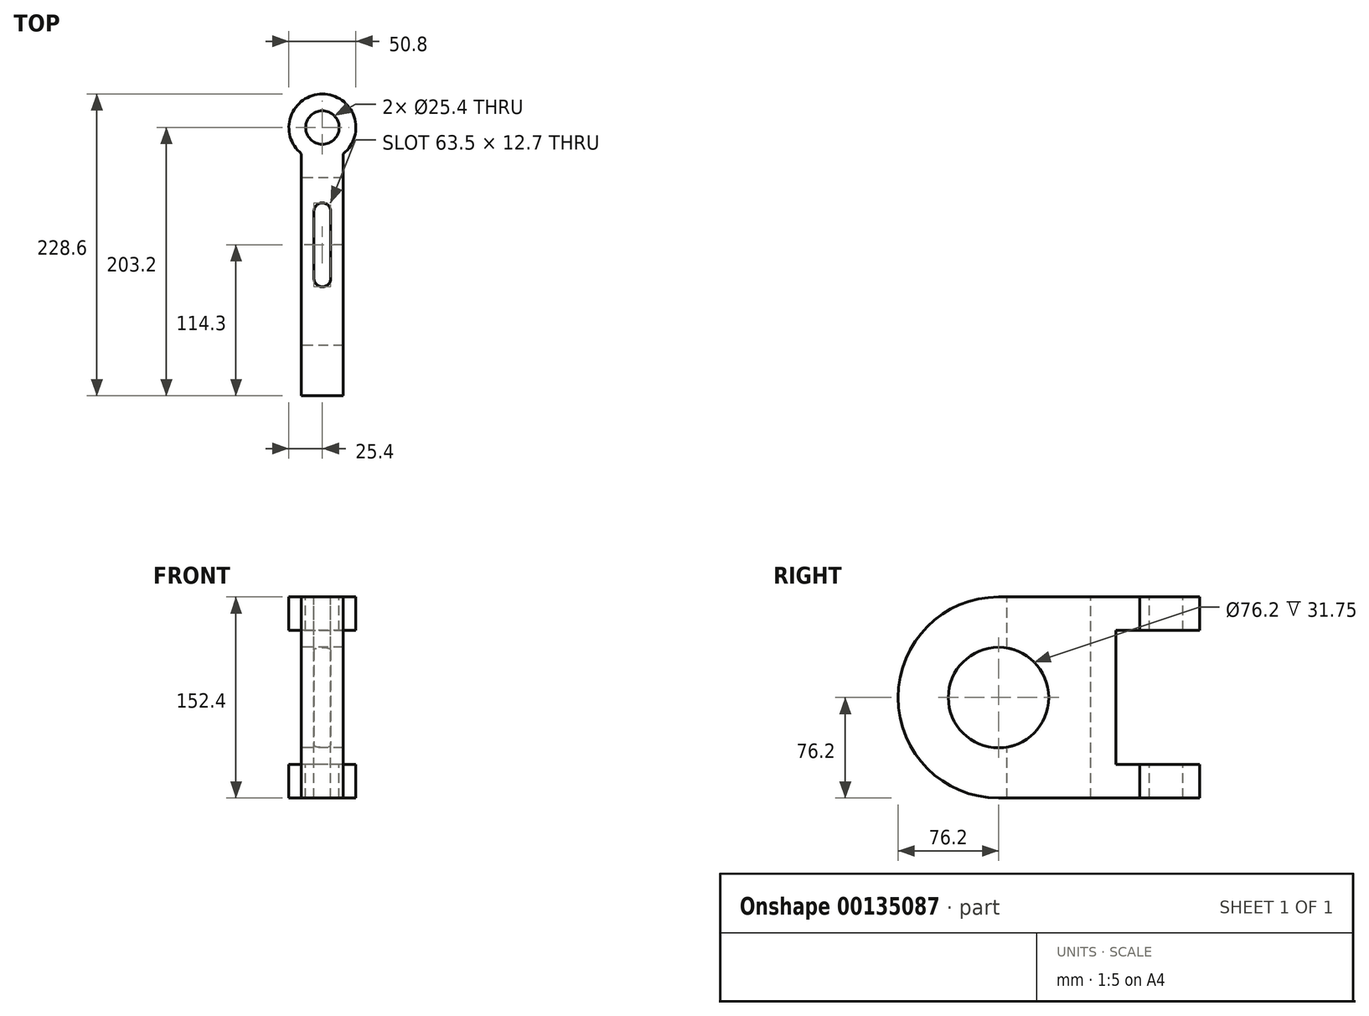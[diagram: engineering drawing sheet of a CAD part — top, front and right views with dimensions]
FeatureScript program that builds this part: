
annotation { "Feature Type Name" : "Feature", "Feature Type Description" : "" }
export const myFeature = defineFeature(function(context is Context, id is Id, definition is map)
    precondition{}
    {
        {
            var Q0;
            Q0=qCreatedBy(makeId("Right.planeOp"),FACE);
            var sketch = newSketch(context, id + "F0", { "sketchPlane" : qUnion([Q0])});
            skCircle(sketch, "E0", {"center": v(0, 0) * mm, "radius": 38.1 * mm});
            skArc(sketch, "E1", {"start": v(0, 76.2) * mm, "mid": v(-76.2, 0) * mm, "end": v(0, -76.2) * mm});
            skPoint(sketch, "E2", {"position": v(88.9, 0) * mm});
            skLineSegment(sketch, "E3", {"start": v(0, 76.2) * mm, "end": v(114.3, 76.2) * mm});
            skLineSegment(sketch, "E4", {"start": v(88.9, 50.8) * mm, "end": v(88.9, -50.8) * mm});
            skLineSegment(sketch, "E5", {"start": v(114.3, 76.2) * mm, "end": v(114.3, 50.8) * mm});
            skLineSegment(sketch, "E6", {"start": v(114.3, 50.8) * mm, "end": v(88.9, 50.8) * mm});
            skLineSegment(sketch, "E7", {"start": v(-76.2, 0) * mm, "end": v(76.2, 0) * mm, "construction": true});
            skLineSegment(sketch, "E8.MirrorCS", {"start": v(114.3, -76.2) * mm, "end": v(114.3, -50.8) * mm});
            skLineSegment(sketch, "E9.MirrorCS", {"start": v(114.3, -50.8) * mm, "end": v(88.9, -50.8) * mm});
            skLineSegment(sketch, "E10.MirrorCS", {"start": v(0, -76.2) * mm, "end": v(114.3, -76.2) * mm});
            skSolve(sketch);
        }
        {
            var Q0;
            Q0 = qSketchRegion(id + "F0", true);
            extrude(context, id + "F1", {"entities" : qUnion([Q0]), "depth" : 15.88 * mm, "hasSecondDirection" : true, "secondDirectionOppositeDirection" : true, "secondDirectionDepth" : 15.88 * mm});
        }
        {
            var Q0;
            Q0=makeQuery(id+"F1.opExtrude","SWEPT_FACE",FACE,{"disambiguationData":[OSD([sQuery(id+"F0.wireOp",EDGE,"E3")])]});
            var sketch = newSketch(context, id + "F2", { "sketchPlane" : qUnion([Q0])});
            skPoint(sketch, "E11", {"position": v(0, 152.4) * mm});
            skPoint(sketch, "E11.positionSnap0", {"position": v(0, 114.3) * mm});
            skPoint(sketch, "E12", {"position": v(0, 127) * mm});
            skArc(sketch, "E13", {"start": v(15.88, 107.17) * mm, "mid": v(0, 152.4) * mm, "end": v(-15.88, 107.17) * mm});
            skCircle(sketch, "E14", {"center": v(0, 127) * mm, "radius": 12.7 * mm});
            skLineSegment(sketch, "E15", {"start": v(-15.88, 107.17) * mm, "end": v(15.88, 107.17) * mm, "construction": true});
            skSolve(sketch);
        }
        {
            var Q0;
            {var subQ8=sQuery(id+"F2.wireOp",EDGE,"E13");Q0=makeQuery(id+"F2.imprint","IMPRINT",FACE,{"disambiguationData":[TD([[makeQuery(id+"F2.imprint","IMPRINT",EDGE,{"derivedFrom":subQ8}),1.0]])]});}
            var Q1;
            Q1=makeQuery(id+"F2.imprint","IMPRINT",FACE,{"disambiguationData":[TD([[makeQuery(id+"F2.imprint","IMPRINT",EDGE,{"derivedFrom":sQuery(id+"F2.wireOp",EDGE,"E14")}),1.0]])]});
            var Q2;
            Q2=sQuery(id+"F2.wireOp",EDGE,"E15");
            var Q3;
            Q3=makeQuery(id+"F1.opExtrude","SWEPT_FACE",FACE,{"disambiguationData":[OSD([sQuery(id+"F0.wireOp",EDGE,"E6")])]});
            extrude(context, id + "F3", {"entities" : qUnion([Q0, Q1]), "operationType" : NewBodyOperationType.ADD, "surfaceEntities" : qUnion([Q2]), "endBound" : BoundingType.UP_TO_SURFACE, "oppositeDirection" : true, "endBoundEntityFace" : qUnion([Q3]), "depth" : 25.4 * mm});
        }
        {
            var Q0;
            Q0=makeQuery(id+"F2.imprint","IMPRINT",FACE,{"disambiguationData":[TD([[makeQuery(id+"F2.imprint","IMPRINT",EDGE,{"derivedFrom":sQuery(id+"F2.wireOp",EDGE,"E14")}),1.0]])]});
            var Q1;
            Q1=makeQuery(id+"F3.boolean.opBoolean","MERGE",FACE,{"derivedFrom":[makeQuery(id+"F1.opExtrude","SWEPT_FACE",FACE,{"disambiguationData":[OSD([sQuery(id+"F0.wireOp",EDGE,"E6")])]}),makeQuery(id+"F3.opExtrude","CAP_FACE",FACE,{"disambiguationData":[OSD([sQuery(id+"F0.wireOp",EDGE,"E3"),sQuery(id+"F0.wireOp",EDGE,"E5"),sQuery(id+"F2.wireOp",EDGE,"E13")])],"isStart":false})]});
            extrude(context, id + "F4", {"entities" : qUnion([Q0]), "operationType" : NewBodyOperationType.REMOVE, "endBound" : BoundingType.UP_TO_SURFACE, "oppositeDirection" : true, "endBoundEntityFace" : qUnion([Q1]), "depth" : 25.4 * mm});
        }
        {
            var Q0;
            Q0=makeQuery(id+"F1.opExtrude","SWEPT_FACE",FACE,{"disambiguationData":[OSD([sQuery(id+"F0.wireOp",EDGE,"E9.MirrorCS")])]});
            var sketch = newSketch(context, id + "F5", { "sketchPlane" : qUnion([Q0])});
            skLineSegment(sketch, "E16.0", {"start": v(15.88, 88.9) * mm, "end": v(-15.88, 88.9) * mm, "construction": true});
            skLineSegment(sketch, "E17.0", {"start": v(15.88, 114.3) * mm, "end": v(-15.88, 114.3) * mm, "construction": true});
            skLineSegment(sketch, "E18.0", {"start": v(15.88, 114.3) * mm, "end": v(15.88, 88.9) * mm, "construction": true});
            skLineSegment(sketch, "E19.0", {"start": v(-15.88, 114.3) * mm, "end": v(-15.88, 88.9) * mm, "construction": true});
            skPoint(sketch, "E20", {"position": v(0, 127) * mm});
            skPoint(sketch, "E20.positionSnap0", {"position": v(0, 114.3) * mm});
            skArc(sketch, "E21", {"start": v(15.88, 107.17) * mm, "mid": v(0, 152.4) * mm, "end": v(-15.88, 107.17) * mm});
            skLineSegment(sketch, "E22", {"start": v(-15.88, 114.3) * mm, "end": v(-22, 114.3) * mm, "construction": true});
            skLineSegment(sketch, "E23", {"start": v(15.88, 114.3) * mm, "end": v(22, 114.3) * mm, "construction": true});
            skSolve(sketch);
        }
        {
            var Q0;
            {var subQ0=sQuery(id+"F5.wireOp",EDGE,"E21");Q0=makeQuery(id+"F5.imprint","IMPRINT",FACE,{"disambiguationData":[TD([[makeQuery(id+"F5.imprint","IMPRINT",EDGE,{"derivedFrom":subQ0}),1.0]])]});}
            var Q1;
            Q1=makeQuery(id+"F1.opExtrude","SWEPT_FACE",FACE,{"disambiguationData":[OSD([sQuery(id+"F0.wireOp",EDGE,"E10.MirrorCS")])]});
            extrude(context, id + "F6", {"entities" : qUnion([Q0]), "operationType" : NewBodyOperationType.ADD, "endBound" : BoundingType.UP_TO_SURFACE, "oppositeDirection" : true, "endBoundEntityFace" : qUnion([Q1]), "depth" : 25.4 * mm});
        }
        {
            var Q0;
            {var subQ0=sQuery(id+"F0.wireOp",EDGE,"E9.MirrorCS");Q0=makeQuery(id+"F6.boolean.opBoolean","MERGE",FACE,{"derivedFrom":[makeQuery(id+"F1.opExtrude","SWEPT_FACE",FACE,{"disambiguationData":[OSD([subQ0])]}),makeQuery(id+"F6.opExtrude","CAP_FACE",FACE,{"disambiguationData":[OSD([sQuery(id+"F0.wireOp",EDGE,"E8.MirrorCS"),subQ0,sQuery(id+"F5.wireOp",EDGE,"E21")])],"isStart":true})]});}
            var sketch = newSketch(context, id + "F7", { "sketchPlane" : qUnion([Q0])});
            skCircle(sketch, "E24.0", {"center": v(0, 127) * mm, "radius": 12.7 * mm});
            skSolve(sketch);
        }
        {
            var Q0;
            Q0 = qSketchRegion(id + "F7", true);
            var Q1;
            Q1=makeQuery(id+"F6.boolean.opBoolean","MERGE",FACE,{"derivedFrom":[makeQuery(id+"F1.opExtrude","SWEPT_FACE",FACE,{"disambiguationData":[OSD([sQuery(id+"F0.wireOp",EDGE,"E10.MirrorCS")])]}),makeQuery(id+"F6.opExtrude","CAP_FACE",FACE,{"disambiguationData":[OSD([sQuery(id+"F0.wireOp",EDGE,"E8.MirrorCS"),sQuery(id+"F0.wireOp",EDGE,"E9.MirrorCS"),sQuery(id+"F5.wireOp",EDGE,"E21")])],"isStart":false})]});
            extrude(context, id + "F8", {"entities" : qUnion([Q0]), "operationType" : NewBodyOperationType.REMOVE, "endBound" : BoundingType.UP_TO_SURFACE, "oppositeDirection" : true, "endBoundEntityFace" : qUnion([Q1]), "depth" : 25.4 * mm});
        }
        {
            var Q0;
            {var subQ0=sQuery(id+"F0.wireOp",EDGE,"E3");Q0=makeQuery(id+"F3.boolean.opBoolean","MERGE",FACE,{"derivedFrom":[makeQuery(id+"F1.opExtrude","SWEPT_FACE",FACE,{"disambiguationData":[OSD([subQ0])]}),makeQuery(id+"F3.opExtrude","CAP_FACE",FACE,{"disambiguationData":[OSD([subQ0,sQuery(id+"F0.wireOp",EDGE,"E5"),sQuery(id+"F2.wireOp",EDGE,"E13")])],"isStart":true})]});}
            var sketch = newSketch(context, id + "F9", { "sketchPlane" : qUnion([Q0])});
            skCircle(sketch, "E25.0", {"center": v(0, 127) * mm, "radius": 12.7 * mm, "construction": true});
            skPoint(sketch, "E26", {"position": v(0, 63.5) * mm});
            skPoint(sketch, "E27", {"position": v(0, 12.7) * mm});
            skArc(sketch, "E28", {"start": v(6.35, 63.5) * mm, "mid": v(0, 69.85) * mm, "end": v(-6.35, 63.5) * mm});
            skArc(sketch, "E29", {"start": v(-6.35, 12.7) * mm, "mid": v(0, 6.35) * mm, "end": v(6.35, 12.7) * mm});
            skLineSegment(sketch, "E30", {"start": v(-6.35, 63.5) * mm, "end": v(-6.35, 12.7) * mm});
            skLineSegment(sketch, "E31", {"start": v(6.35, 63.5) * mm, "end": v(6.35, 12.7) * mm});
            skSolve(sketch);
        }
        {
            var Q0;
            Q0 = qSketchRegion(id + "F9", true);
            var Q1;
            Q1=makeQuery(id+"F6.boolean.opBoolean","MERGE",FACE,{"derivedFrom":[makeQuery(id+"F1.opExtrude","SWEPT_FACE",FACE,{"disambiguationData":[OSD([sQuery(id+"F0.wireOp",EDGE,"E10.MirrorCS")])]}),makeQuery(id+"F6.opExtrude","CAP_FACE",FACE,{"disambiguationData":[OSD([sQuery(id+"F0.wireOp",EDGE,"E8.MirrorCS"),sQuery(id+"F0.wireOp",EDGE,"E9.MirrorCS"),sQuery(id+"F5.wireOp",EDGE,"E21")])],"isStart":false})]});
            extrude(context, id + "F10", {"entities" : qUnion([Q0]), "operationType" : NewBodyOperationType.REMOVE, "endBound" : BoundingType.UP_TO_SURFACE, "oppositeDirection" : true, "endBoundEntityFace" : qUnion([Q1]), "depth" : 97.32 * mm});
        }
    });
